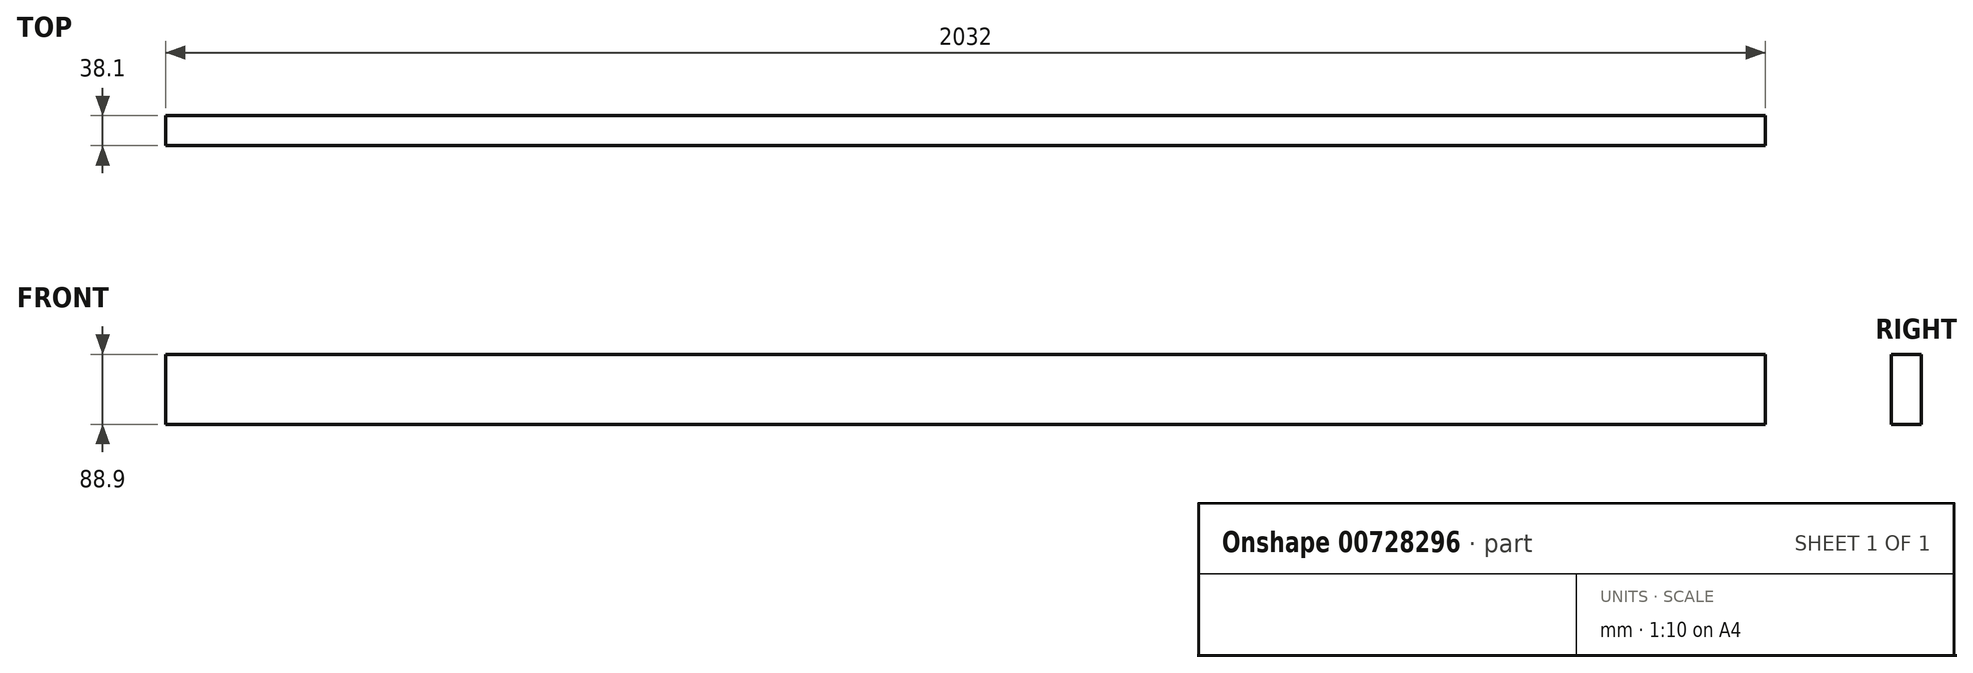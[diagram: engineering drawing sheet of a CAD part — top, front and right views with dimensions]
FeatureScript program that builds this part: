
annotation { "Feature Type Name" : "Feature", "Feature Type Description" : "" }
export const myFeature = defineFeature(function(context is Context, id is Id, definition is map)
    precondition{}
    {
        {
            var Q0;
            Q0=qCreatedBy(makeId("Front.planeOp"),FACE);
            var sketch = newSketch(context, id + "F0", { "sketchPlane" : qUnion([Q0])});
            skLineSegment(sketch, "E0.bottom", {"start": v(-1016, -44.45) * mm, "end": v(1016, -44.45) * mm});
            skLineSegment(sketch, "E0.top", {"start": v(-1016, 44.45) * mm, "end": v(1016, 44.45) * mm});
            skLineSegment(sketch, "E0.left", {"start": v(-1016, -44.45) * mm, "end": v(-1016, 44.45) * mm});
            skLineSegment(sketch, "E0.right", {"start": v(1016, -44.45) * mm, "end": v(1016, 44.45) * mm});
            skPoint(sketch, "E0.middle", {"position": v(0, 0) * mm});
            skSolve(sketch);
        }
        {
            var Q0;
            Q0=qSketchRegion(id+"F0",true);
            extrude(context, id + "F1", {"entities" : qUnion([Q0]), "depth" : 38.1 * mm, "offsetDistance" : 25.4 * mm});
        }
    });
